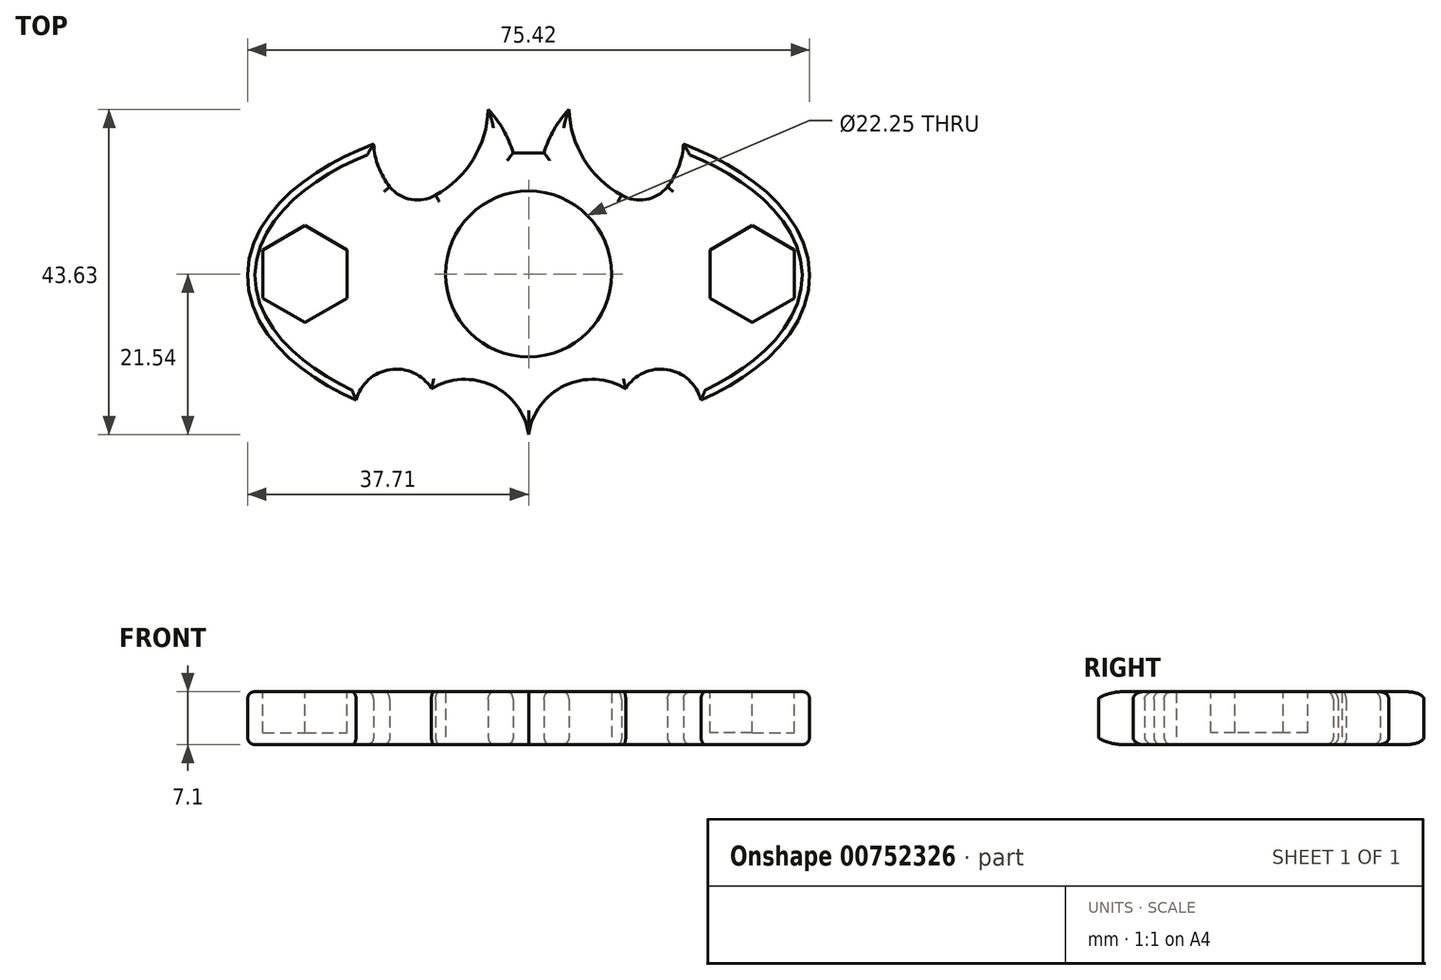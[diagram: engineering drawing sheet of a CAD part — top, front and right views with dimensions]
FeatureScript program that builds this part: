
annotation { "Feature Type Name" : "Feature", "Feature Type Description" : "" }
export const myFeature = defineFeature(function(context is Context, id is Id, definition is map)
    precondition{}
    {
        {
            var Q0;
            Q0=qCreatedBy(makeId("Top.planeOp"),FACE);
            var sketch = newSketch(context, id + "F0", { "sketchPlane" : qUnion([Q0])});
            skCircle(sketch, "E0", {"center": v(0, 0) * mm, "radius": 11.12 * mm});
            skCircle(sketch, "E1", {"center": v(0, 0) * mm, "radius": 15 * mm});
            skSolve(sketch);
        }
        {
            var Q0;
            Q0=qSketchRegion(id+"F0",true);
            extrude(context, id + "F1", {"entities" : qUnion([Q0]), "depth" : 7.1 * mm, "offsetDistance" : 25 * mm});
        }
        {
            var Q0;
            Q0=qCreatedBy(makeId("Top.planeOp"),FACE);
            var sketch = newSketch(context, id + "F2", { "sketchPlane" : qUnion([Q0])});
            skArc(sketch, "E2", {"start": v(-13.03, -15.38) * mm, "mid": v(-18.59, -12.82) * mm, "end": v(-23.12, -16.92) * mm});
            skArc(sketch, "E3", {"start": v(-0.5, -19.64) * mm, "mid": v(-5.77, -14.6) * mm, "end": v(-13.03, -15.38) * mm});
            skArc(sketch, "E4", {"start": v(-12.46, 10.57) * mm, "mid": v(-7.42, 15.4) * mm, "end": v(-5.42, 22.09) * mm});
            skArc(sketch, "E5", {"start": v(-2.08, 16.24) * mm, "mid": v(-3.4, 19.37) * mm, "end": v(-5.42, 22.09) * mm});
            skArc(sketch, "E6", {"start": v(-20.8, 17.41) * mm, "mid": v(-20.14, 14.39) * mm, "end": v(-18.62, 11.68) * mm});
            skLineSegment(sketch, "E7", {"start": v(-2.08, 16.24) * mm, "end": v(0, 16.24) * mm});
            skEllipticalArc(sketch, "E8", {});
            skPoint(sketch, "E9.orphan", {"position": v(-20.7, 16.6) * mm});
            skArc(sketch, "E10", {"start": v(0, -21.54) * mm, "mid": v(-4.86, -14.96) * mm, "end": v(-13.03, -15.38) * mm});
            skLineSegment(sketch, "E11", {"start": v(0, -21.54) * mm, "end": v(0, -21.54) * mm});
            skArc(sketch, "E12", {"start": v(-18.62, 11.68) * mm, "mid": v(-15.74, 10) * mm, "end": v(-12.46, 10.57) * mm});
            skLineSegment(sketch, "E13.MirrorCS", {"start": v(2.08, 16.24) * mm, "end": v(0, 16.24) * mm});
            skEllipticalArc(sketch, "E14.MirrorCS", {});
            skArc(sketch, "E15.MirrorCS", {"start": v(0.5, -19.64) * mm, "mid": v(5.77, -14.6) * mm, "end": v(13.03, -15.38) * mm});
            skArc(sketch, "E16.MirrorCS", {"start": v(0, -21.54) * mm, "mid": v(4.86, -14.96) * mm, "end": v(13.03, -15.38) * mm});
            skArc(sketch, "E17.MirrorCS", {"start": v(13.03, -15.38) * mm, "mid": v(18.59, -12.82) * mm, "end": v(23.12, -16.92) * mm});
            skArc(sketch, "E18.MirrorCS", {"start": v(20.8, 17.41) * mm, "mid": v(20.14, 14.39) * mm, "end": v(18.62, 11.68) * mm});
            skArc(sketch, "E19.MirrorCS", {"start": v(12.46, 10.57) * mm, "mid": v(7.42, 15.4) * mm, "end": v(5.42, 22.09) * mm});
            skArc(sketch, "E20.MirrorCS", {"start": v(2.08, 16.24) * mm, "mid": v(3.4, 19.37) * mm, "end": v(5.42, 22.09) * mm});
            skPoint(sketch, "E21.MirrorP", {"position": v(20.7, 16.6) * mm});
            skArc(sketch, "E22.MirrorCS", {"start": v(18.62, 11.68) * mm, "mid": v(15.74, 10) * mm, "end": v(12.46, 10.57) * mm});
            skCircle(sketch, "E23", {"center": v(0, 0) * mm, "radius": 11.12 * mm});
            const initialGuessF2  = {"E8": [0.0021673258622125304, -0.00023363387563712012, 1, 0, 0.039878606296580424, 0.02158404547153654, 2.18441789660064, 4.025396672470418], "E14.MirrorCS": [-0.0021673258622125304, -0.00023363387563712012, -1, 0, 0.039878606296580424, 0.02158404547153654, 2.2577886347091685, 4.0987674105789464]};
            skSetInitialGuess(sketch, initialGuessF2);
            skSolve(sketch);
        }
        {
            var Q0;
            Q0 = qSketchRegion(id + "F2", true);
            extrude(context, id + "F3", {"entities" : qUnion([Q0]), "operationType" : NewBodyOperationType.ADD, "depth" : 7.1 * mm, "offsetDistance" : 25 * mm});
        }
        {
            var Q0;
            Q0=makeQuery(id+"F3.boolean.opBoolean","MERGE",FACE,{"derivedFrom":[makeQuery(id+"F1.opExtrude","CAP_FACE",FACE,{"disambiguationData":[OSD([sQuery(id+"F0.wireOp",EDGE,"E0"),sQuery(id+"F0.wireOp",EDGE,"E1")])],"isStart":false}),makeQuery(id+"F3.opExtrude","CAP_FACE",FACE,{"disambiguationData":[OSD([sQuery(id+"F2.wireOp",EDGE,"E2"),sQuery(id+"F2.wireOp",EDGE,"E4"),sQuery(id+"F2.wireOp",EDGE,"E5"),sQuery(id+"F2.wireOp",EDGE,"E6"),sQuery(id+"F2.wireOp",EDGE,"E7"),sQuery(id+"F2.wireOp",EDGE,"E8"),sQuery(id+"F2.wireOp",EDGE,"E10"),sQuery(id+"F2.wireOp",EDGE,"E12"),sQuery(id+"F2.wireOp",EDGE,"E13.MirrorCS"),sQuery(id+"F2.wireOp",EDGE,"E14.MirrorCS"),sQuery(id+"F2.wireOp",EDGE,"E16.MirrorCS"),sQuery(id+"F2.wireOp",EDGE,"E17.MirrorCS"),sQuery(id+"F2.wireOp",EDGE,"E18.MirrorCS"),sQuery(id+"F2.wireOp",EDGE,"E19.MirrorCS"),sQuery(id+"F2.wireOp",EDGE,"E20.MirrorCS"),sQuery(id+"F2.wireOp",EDGE,"E22.MirrorCS"),sQuery(id+"F2.wireOp",EDGE,"E23")])],"isStart":false})]});
            var sketch = newSketch(context, id + "F4", { "sketchPlane" : qUnion([Q0])});
            skCircle(sketch, "E24.cCircle", {"center": v(-30, 0) * mm, "radius": 5.62 * mm, "construction": true});
            skLineSegment(sketch, "E24.0", {"start": v(-24.38, 3.25) * mm, "end": v(-24.38, -3.25) * mm});
            skLineSegment(sketch, "E24.1", {"start": v(-24.38, -3.25) * mm, "end": v(-30, -6.5) * mm});
            skLineSegment(sketch, "E24.2", {"start": v(-30, -6.5) * mm, "end": v(-35.62, -3.25) * mm});
            skLineSegment(sketch, "E24.3", {"start": v(-35.62, -3.25) * mm, "end": v(-35.62, 3.25) * mm});
            skLineSegment(sketch, "E24.4", {"start": v(-35.63, 3.25) * mm, "end": v(-30, 6.5) * mm});
            skLineSegment(sketch, "E24.5", {"start": v(-30, 6.5) * mm, "end": v(-24.38, 3.25) * mm});
            skPoint(sketch, "E24.0.midPoint", {"position": v(-24.38, 0) * mm});
            skLineSegment(sketch, "E25.MirrorCS", {"start": v(24.38, 3.25) * mm, "end": v(24.38, -3.25) * mm});
            skLineSegment(sketch, "E26.MirrorCS", {"start": v(24.38, -3.25) * mm, "end": v(30, -6.5) * mm});
            skLineSegment(sketch, "E27.MirrorCS", {"start": v(30, -6.5) * mm, "end": v(35.62, -3.25) * mm});
            skLineSegment(sketch, "E28.MirrorCS", {"start": v(35.62, -3.25) * mm, "end": v(35.62, 3.25) * mm});
            skLineSegment(sketch, "E29.MirrorCS", {"start": v(35.62, 3.25) * mm, "end": v(30, 6.5) * mm});
            skLineSegment(sketch, "E30.MirrorCS", {"start": v(30, 6.5) * mm, "end": v(24.38, 3.25) * mm});
            skCircle(sketch, "E31.MirrorC", {"center": v(30, 0) * mm, "radius": 5.62 * mm, "construction": true});
            skPoint(sketch, "E32.MirrorP", {"position": v(24.38, 0) * mm});
            skSolve(sketch);
        }
        {
            var Q0;
            Q0 = qSketchRegion(id + "F4", true);
            extrude(context, id + "F5", {"entities" : qUnion([Q0]), "operationType" : NewBodyOperationType.REMOVE, "oppositeDirection" : true, "depth" : 5.5 * mm, "offsetDistance" : 25 * mm});
        }
        {
            var Q0;
            Q0=makeQuery(id+"F3.opExtrude","CAP_EDGE",EDGE,{"disambiguationData":[OSD([sQuery(id+"F2.wireOp",EDGE,"E8")])],"isStart":false});
            var Q1;
            Q1=makeQuery(id+"F3.opExtrude","CAP_EDGE",EDGE,{"disambiguationData":[OSD([sQuery(id+"F2.wireOp",EDGE,"E2")])],"isStart":false});
            var Q2;
            Q2=makeQuery(id+"F3.opExtrude","CAP_EDGE",EDGE,{"disambiguationData":[OSD([sQuery(id+"F2.wireOp",EDGE,"E10")])],"isStart":false});
            var Q3;
            Q3=makeQuery(id+"F3.opExtrude","CAP_EDGE",EDGE,{"disambiguationData":[OSD([sQuery(id+"F2.wireOp",EDGE,"E16.MirrorCS")])],"isStart":false});
            var Q4;
            Q4=makeQuery(id+"F3.opExtrude","CAP_EDGE",EDGE,{"disambiguationData":[OSD([sQuery(id+"F2.wireOp",EDGE,"E17.MirrorCS")])],"isStart":false});
            var Q5;
            Q5=makeQuery(id+"F3.opExtrude","CAP_EDGE",EDGE,{"disambiguationData":[OSD([sQuery(id+"F2.wireOp",EDGE,"E14.MirrorCS")])],"isStart":false});
            var Q6;
            Q6=makeQuery(id+"F3.opExtrude","CAP_EDGE",EDGE,{"disambiguationData":[OSD([sQuery(id+"F2.wireOp",EDGE,"E22.MirrorCS")])],"isStart":false});
            var Q7;
            Q7=makeQuery(id+"F3.opExtrude","CAP_EDGE",EDGE,{"disambiguationData":[OSD([sQuery(id+"F2.wireOp",EDGE,"E18.MirrorCS")])],"isStart":false});
            var Q8;
            Q8=makeQuery(id+"F3.opExtrude","CAP_EDGE",EDGE,{"disambiguationData":[OSD([sQuery(id+"F2.wireOp",EDGE,"E19.MirrorCS")])],"isStart":false});
            var Q9;
            Q9=makeQuery(id+"F3.opExtrude","CAP_EDGE",EDGE,{"disambiguationData":[OSD([sQuery(id+"F2.wireOp",EDGE,"E20.MirrorCS")])],"isStart":false});
            var Q10;
            Q10=makeQuery(id+"F3.opExtrude","CAP_EDGE",EDGE,{"disambiguationData":[OSD([sQuery(id+"F2.wireOp",EDGE,"E7"),sQuery(id+"F2.wireOp",EDGE,"E13.MirrorCS")])],"isStart":false});
            var Q11;
            Q11=makeQuery(id+"F3.opExtrude","CAP_EDGE",EDGE,{"disambiguationData":[OSD([sQuery(id+"F2.wireOp",EDGE,"E5")])],"isStart":false});
            var Q12;
            Q12=makeQuery(id+"F3.opExtrude","CAP_EDGE",EDGE,{"disambiguationData":[OSD([sQuery(id+"F2.wireOp",EDGE,"E4")])],"isStart":false});
            var Q13;
            Q13=makeQuery(id+"F3.opExtrude","CAP_EDGE",EDGE,{"disambiguationData":[OSD([sQuery(id+"F2.wireOp",EDGE,"E6")])],"isStart":false});
            fillet(context, id + "F6", {"entities" : qUnion([Q0, Q1, Q2, Q3, Q4, Q5, Q6, Q7, Q8, Q9, Q10, Q11, Q12, Q13]), "radius" : 1 * mm, "tangentPropagation" : true, "allowEdgeOverflow" : false});
        }
        {
            var Q0;
            Q0=makeQuery(id+"F3.opExtrude","CAP_EDGE",EDGE,{"disambiguationData":[OSD([sQuery(id+"F2.wireOp",EDGE,"E14.MirrorCS")])],"isStart":true});
            var Q1;
            Q1=makeQuery(id+"F3.opExtrude","CAP_EDGE",EDGE,{"disambiguationData":[OSD([sQuery(id+"F2.wireOp",EDGE,"E17.MirrorCS")])],"isStart":true});
            var Q2;
            Q2=makeQuery(id+"F3.opExtrude","CAP_EDGE",EDGE,{"disambiguationData":[OSD([sQuery(id+"F2.wireOp",EDGE,"E16.MirrorCS")])],"isStart":true});
            var Q3;
            Q3=makeQuery(id+"F3.opExtrude","CAP_EDGE",EDGE,{"disambiguationData":[OSD([sQuery(id+"F2.wireOp",EDGE,"E10")])],"isStart":true});
            var Q4;
            Q4=makeQuery(id+"F3.opExtrude","CAP_EDGE",EDGE,{"disambiguationData":[OSD([sQuery(id+"F2.wireOp",EDGE,"E2")])],"isStart":true});
            var Q5;
            Q5=makeQuery(id+"F3.opExtrude","CAP_EDGE",EDGE,{"disambiguationData":[OSD([sQuery(id+"F2.wireOp",EDGE,"E8")])],"isStart":true});
            var Q6;
            Q6=makeQuery(id+"F3.opExtrude","CAP_EDGE",EDGE,{"disambiguationData":[OSD([sQuery(id+"F2.wireOp",EDGE,"E6")])],"isStart":true});
            var Q7;
            Q7=makeQuery(id+"F3.opExtrude","CAP_EDGE",EDGE,{"disambiguationData":[OSD([sQuery(id+"F2.wireOp",EDGE,"E12")])],"isStart":true});
            var Q8;
            Q8=makeQuery(id+"F3.opExtrude","CAP_EDGE",EDGE,{"disambiguationData":[OSD([sQuery(id+"F2.wireOp",EDGE,"E4")])],"isStart":true});
            var Q9;
            Q9=makeQuery(id+"F3.opExtrude","CAP_EDGE",EDGE,{"disambiguationData":[OSD([sQuery(id+"F2.wireOp",EDGE,"E5")])],"isStart":true});
            var Q10;
            Q10=makeQuery(id+"F3.opExtrude","CAP_EDGE",EDGE,{"disambiguationData":[OSD([sQuery(id+"F2.wireOp",EDGE,"E7"),sQuery(id+"F2.wireOp",EDGE,"E13.MirrorCS")])],"isStart":true});
            var Q11;
            Q11=makeQuery(id+"F3.opExtrude","CAP_EDGE",EDGE,{"disambiguationData":[OSD([sQuery(id+"F2.wireOp",EDGE,"E20.MirrorCS")])],"isStart":true});
            var Q12;
            Q12=makeQuery(id+"F3.opExtrude","CAP_EDGE",EDGE,{"disambiguationData":[OSD([sQuery(id+"F2.wireOp",EDGE,"E19.MirrorCS")])],"isStart":true});
            var Q13;
            Q13=makeQuery(id+"F3.opExtrude","CAP_EDGE",EDGE,{"disambiguationData":[OSD([sQuery(id+"F2.wireOp",EDGE,"E18.MirrorCS")])],"isStart":true});
            fillet(context, id + "F7", {"entities" : qUnion([Q0, Q1, Q2, Q3, Q4, Q5, Q6, Q7, Q8, Q9, Q10, Q11, Q12, Q13]), "radius" : 1 * mm, "tangentPropagation" : true, "allowEdgeOverflow" : false});
        }
    });
